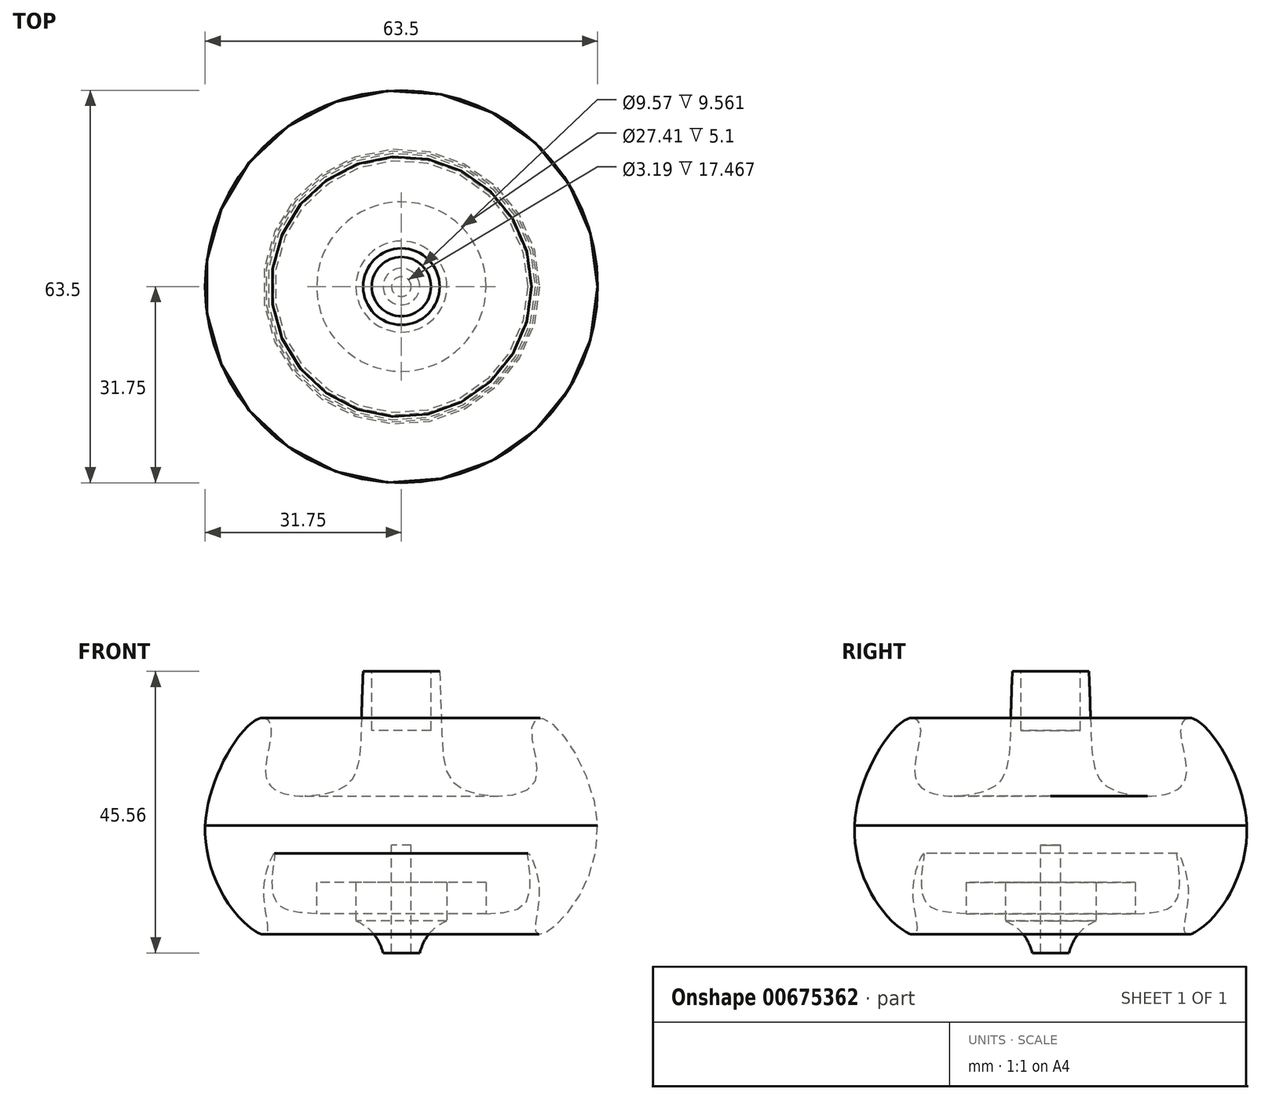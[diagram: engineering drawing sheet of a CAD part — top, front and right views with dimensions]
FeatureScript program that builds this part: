
annotation { "Feature Type Name" : "Feature", "Feature Type Description" : "" }
export const myFeature = defineFeature(function(context is Context, id is Id, definition is map)
    precondition{}
    {
        {
            var Q0;
            Q0=qCreatedBy(makeId("Front.planeOp"),FACE);
            var sketch = newSketch(context, id + "F0", { "sketchPlane" : qUnion([Q0])});
            skLineSegment(sketch, "E0", {"start": v(1.6, 0) * mm, "end": v(1.6, 17.47) * mm});
            skLineSegment(sketch, "E1", {"start": v(1.6, 17.47) * mm, "end": v(0, 17.47) * mm});
            skLineSegment(sketch, "E2", {"start": v(1.6, 0) * mm, "end": v(2.96, 0) * mm});
            skLineSegment(sketch, "E3", {"start": v(0, 20.62) * mm, "end": v(0, 17.47) * mm});
            skPoint(sketch, "E4.startSnap0", {"position": v(1.6, 8.73) * mm});
            skFitSpline(sketch, "E5", {"points": [v(2.96, 0) * mm, v(19.85, 7.8) * mm, v(20.46, 16.08) * mm, v(22.3, 10.4) * mm, v(22, 3.05) * mm, v(31.74, 20.62) * mm], "startDerivative": vector(29.91, 106.76) * mm, "endDerivative": vector(-4.2, 122.77) * mm});
            skLineSegment(sketch, "E6", {"start": v(0, 36) * mm, "end": v(4.79, 36) * mm});
            skLineSegment(sketch, "E7", {"start": v(4.79, 36) * mm, "end": v(4.79, 45.56) * mm});
            skLineSegment(sketch, "E8", {"start": v(4.79, 45.56) * mm, "end": v(6.18, 45.56) * mm});
            skFitSpline(sketch, "E9", {"points": [v(6.18, 45.56) * mm, v(10.1, 26.4) * mm, v(21.38, 27.27) * mm, v(21.07, 36) * mm, v(22.76, 38) * mm, v(31.74, 20.62) * mm], "startDerivative": vector(7.41, -148.24) * mm, "endDerivative": vector(4.55, -93.81) * mm});
            skLineSegment(sketch, "E10", {"start": v(0, 36) * mm, "end": v(0, 20.62) * mm});
            skSolve(sketch);
        }
        {
            var Q0;
            Q0=makeQuery(id+"F0.imprint","IMPRINT",FACE,{"disambiguationData":[TD([[makeQuery(id+"F0.imprint","IMPRINT",EDGE,{"derivedFrom":sQuery(id+"F0.wireOp",EDGE,"E0")}),-1.0]])]});
            var Q1;
            Q1=sQuery(id+"F0.wireOp",EDGE,"E10");
            revolve(context, id + "F1", {"entities" : qUnion([Q0]), "axis" : qUnion([Q1]), "revolveType" : RevolveType.FULL});
        }
        {
            var Q0;
            Q0=qCreatedBy(makeId("Top.planeOp"),FACE);
            var sketch = newSketch(context, id + "F2", { "sketchPlane" : qUnion([Q0])});
            skCircle(sketch, "E11", {"center": v(0, 0) * mm, "radius": 13.7 * mm});
            skCircle(sketch, "E12", {"center": v(0, 0) * mm, "radius": 7.36 * mm});
            skSolve(sketch);
        }
        {
            var Q0;
            Q0 = qSketchRegion(id + "F2", true);
            extrude(context, id + "F3", {"entities" : qUnion([Q0]), "operationType" : NewBodyOperationType.REMOVE, "depth" : 11.43 * mm, "offsetDistance" : 25.4 * mm});
        }
    });
